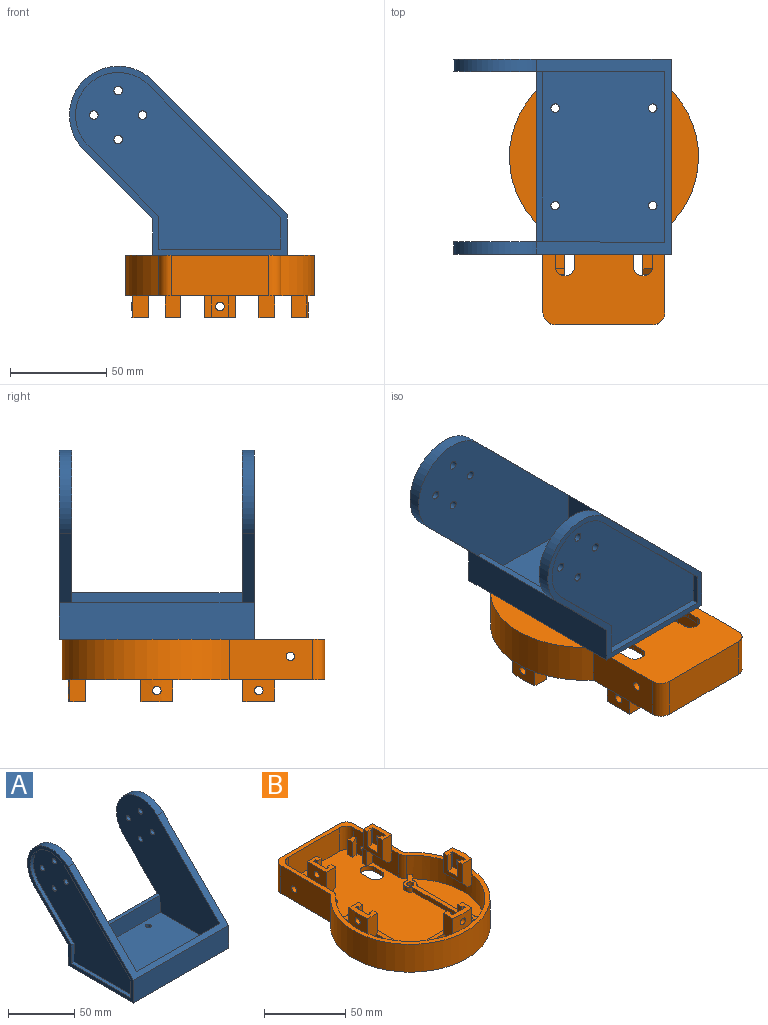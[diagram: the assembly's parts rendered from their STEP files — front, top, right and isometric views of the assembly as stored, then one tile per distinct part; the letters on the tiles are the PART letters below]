
ASSEMBLY  parts=2 mates=1
PART A: 42 faces, bbox 101.5x113.3x98.4 mm
  f0: plane 106.95x92.08mm, normal (-1,0,0), area 5115.5mm2, adj f15,f16,f17,f18,f35,f36,f37,f38
  f1: plane 101.47x69.94mm, normal (0,-0.71,0.71), area 1654.8mm2, adj f6,f9,f12,f13,f23,f24,f34,f41
  f2: plane 36.01x36.01mm, normal (0,0.71,-0.71), area 323.4mm2, adj f6,f9,f27,f34
  f3: cylinder r=2.22mm len=4.45mm, axis (-1,0,0), area 44.3mm2, adj f8,f9
  f4: cylinder r=2.22mm len=4.45mm, axis (-1,0,0), area 44.3mm2, adj f8,f9
  f5: cylinder r=2.22mm len=4.45mm, axis (-1,0,0), area 44.3mm2, adj f8,f9
  f6: cylinder r=25.4mm len=43.36mm, axis (-1,0,0), area 506.7mm2, adj f1,f2,f9,f34
  f7: cylinder r=2.22mm len=4.45mm, axis (-1,0,0), area 44.3mm2, adj f8,f9
  f8: plane 106.95x92.08mm, normal (1,0,0), area 5115.5mm2, adj f3,f4,f5,f7,f28,f29,f30,f31
  f9: plane 110.13x95.25mm, normal (-1,0,0), area 5823.7mm2, adj f1,f2,f3,f4,f5,f6,f7,f10
  f10: plane 88.77x63.5mm, normal (0,0,1), area 5575mm2, adj f9,f12,f19,f20,f21,f22,f23,f25
  f11: plane 101.47x69.85mm, normal (0,0,-1), area 7025.8mm2, adj f19,f20,f21,f22,f24,f27,f34,f41
  f12: plane 110.13x95.25mm, normal (1,0,0), area 5823.7mm2, adj f1,f10,f13,f14,f15,f16,f17,f18
  f13: cylinder r=25.4mm len=43.36mm, axis (-1,0,0), area 506.7mm2, adj f1,f12,f14,f41
  f14: plane 36.01x36.01mm, normal (0,0.71,-0.71), area 323.4mm2, adj f12,f13,f27,f41
  f15: cylinder r=2.22mm len=4.45mm, axis (-1,0,0), area 44.3mm2, adj f0,f12
  f16: cylinder r=2.22mm len=4.45mm, axis (-1,0,0), area 44.3mm2, adj f0,f12
  f17: cylinder r=2.22mm len=4.45mm, axis (-1,0,0), area 44.3mm2, adj f0,f12
  f18: cylinder r=2.22mm len=4.45mm, axis (-1,0,0), area 44.3mm2, adj f0,f12
  f19: cylinder r=2.22mm len=4.45mm, axis (0,0,1), area 44.3mm2, adj f10,f11
  f20: cylinder r=2.22mm len=4.45mm, axis (0,0,1), area 44.3mm2, adj f10,f11
  f21: cylinder r=2.22mm len=4.45mm, axis (0,0,1), area 44.3mm2, adj f10,f11
  f22: cylinder r=2.22mm len=4.45mm, axis (0,0,1), area 44.3mm2, adj f10,f11
  f23: plane 88.77x21.04mm, normal (0,1,0), area 1868mm2, adj f1,f9,f10,f12
  f24: plane 101.47x21.04mm, normal (0,-1,0), area 2135.2mm2, adj f1,f11,f34,f41
  f25: plane 88.77x15.88mm, normal (0,-1,0), area 1409.3mm2, adj f9,f10,f12,f26
  f26: plane 88.77x3.18mm, normal (0,0,1), area 281.9mm2, adj f9,f12,f25,f27
  f27: plane 101.47x19.05mm, normal (0,1,0), area 1933.1mm2, adj f2,f11,f14,f26,f34,f41
  f28: plane 36.94x36.94mm, normal (0,-0.71,0.71), area 165.9mm2, adj f8,f29,f33,f34
  f29: plane 17.19x3.18mm, normal (0,-1,0), area 54.6mm2, adj f8,f28,f30,f34
  f30: plane 63.5x3.18mm, normal (0,0,1), area 201.6mm2, adj f8,f29,f31,f34
  f31: plane 16.55x3.18mm, normal (0,1,0), area 52.6mm2, adj f8,f30,f32,f34
  f32: plane 69.01x69.01mm, normal (0,0.71,-0.71), area 309.9mm2, adj f8,f31,f33,f34
  f33: cylinder r=22.23mm len=37.94mm, axis (-1,0,0), area 221.7mm2, adj f8,f28,f32,f34
  f34: plane 113.3x98.43mm, normal (1,0,0), area 1042.2mm2, adj f1,f2,f6,f11,f24,f27,f28,f29
  f35: plane 17.19x3.18mm, normal (0,-1,0), area 54.6mm2, adj f0,f36,f40,f41
  f36: plane 36.94x36.94mm, normal (0,-0.71,0.71), area 165.9mm2, adj f0,f35,f37,f41
  f37: cylinder r=22.23mm len=37.94mm, axis (1,0,0), area 221.7mm2, adj f0,f36,f38,f41
  f38: plane 69.01x69.01mm, normal (0,0.71,-0.71), area 309.9mm2, adj f0,f37,f39,f41
  f39: plane 16.55x3.18mm, normal (0,1,0), area 52.6mm2, adj f0,f38,f40,f41
  f40: plane 63.5x3.18mm, normal (0,0,1), area 201.6mm2, adj f0,f35,f39,f41
  f41: plane 113.3x98.43mm, normal (-1,0,0), area 1042.2mm2, adj f1,f11,f13,f14,f24,f27,f35,f36
PART B: 190 faces, bbox 98.4x136.6x32.4 mm
  f0: plane 11.43x5.08mm, normal (0,0,1), area 49.7mm2, adj f7,f176,f178,f179,f180,f181,f182,f183
  f1: plane 136.59x98.43mm, normal (0,0,1), area 1242.6mm2, adj f11,f13,f15,f19,f20,f21,f25,f28
  f2: plane 11.43x5.08mm, normal (0,0,1), area 49.7mm2, adj f97,f167,f169,f170,f171,f172,f173,f174
  f3: plane 11.43x5.08mm, normal (0,0,1), area 49.7mm2, adj f9,f158,f160,f161,f162,f163,f164,f165
  f4: plane 11.43x5.08mm, normal (0,0,1), area 49.7mm2, adj f107,f149,f151,f152,f153,f154,f155,f156
  f5: plane 11.43x5.08mm, normal (0,0,1), area 49.7mm2, adj f10,f140,f142,f143,f144,f145,f146,f147
  f6: plane 3.18x3.18mm, normal (0,0,-1), area 10.1mm2, adj f11,f99,f128,f138
  f7: plane 16.51x14.61mm, normal (-1,0,0), area 139.5mm2, adj f0,f99,f100,f129,f138,f139,f176,f178
  f8: plane 3.18x3.18mm, normal (0,0,-1), area 10.1mm2, adj f13,f77,f125,f137
  f9: plane 16.51x14.61mm, normal (-1,0,0), area 139.5mm2, adj f3,f109,f110,f118,f130,f131,f158,f160
  f10: plane 16.51x14.61mm, normal (1,0,0), area 139.5mm2, adj f5,f102,f103,f113,f134,f135,f140,f142
  f11: plane 22.29x17.78mm, normal (-1,0,0), area 311.7mm2, adj f1,f6,f12,f14,f34,f99,f101,f127
  f12: plane 11.43x5.08mm, normal (0,-1,0), area 50.2mm2, adj f11,f14,f85,f101,f139
  f13: plane 22.29x17.78mm, normal (1,0,0), area 311.7mm2, adj f1,f8,f14,f33,f77,f96,f98,f124
  f14: plane 108.01x62.82mm, normal (0,0,1), area 5270.4mm2, adj f11,f12,f13,f15,f28,f29,f30,f31
  f15: plane 17.78x16.51mm, normal (-1,0,0), area 220mm2, adj f1,f14,f31,f82,f86,f87,f92,f94
  f16: plane 136.59x98.43mm, normal (0,0,-1), area 9894.2mm2, adj f19,f20,f21,f22,f23,f24,f25,f26
  f17: plane 62.82x19.05mm, normal (0,0,1), area 892.1mm2, adj f28,f37,f38,f39,f40,f41
  f18: plane 62.82x19.05mm, normal (0,0,1), area 892.1mm2, adj f28,f42,f43,f44,f45,f46
  f19: plane 43.43x20.96mm, normal (-1,0,0), area 894.5mm2, adj f1,f16,f20,f36,f93
  f20: cylinder r=49.21mm len=98.43mm, axis (0,0,-1), area 5033.2mm2, adj f1,f16,f19,f21
  f21: plane 43.43x20.96mm, normal (1,0,0), area 894.5mm2, adj f1,f16,f20,f35,f94
  f22: cylinder r=2.22mm len=6.35mm, axis (0,0,-1), area 88.7mm2, adj f16,f61
  f23: cylinder r=2.22mm len=6.35mm, axis (0,0,-1), area 88.7mm2, adj f16,f61
  f24: cylinder r=2.22mm len=6.35mm, axis (0,0,-1), area 88.7mm2, adj f16,f61
  f25: plane 50.8x20.96mm, normal (0,1,0), area 1064.5mm2, adj f1,f16,f35,f36
  f26: cylinder r=2.22mm len=6.35mm, axis (0,0,-1), area 88.7mm2, adj f16,f61
  f27: plane 62.82x19.05mm, normal (0,0,1), area 892.1mm2, adj f28,f56,f57,f58,f59,f60
  f28: cylinder r=46.04mm len=92.08mm, axis (0,0,-1), area 3497mm2, adj f1,f14,f17,f18,f27,f33,f34,f37
  f29: plane 17.78x16.51mm, normal (1,0,0), area 220mm2, adj f1,f14,f32,f71,f75,f76,f81,f93
  f30: plane 44.45x17.78mm, normal (0,-1,0), area 790.3mm2, adj f1,f14,f31,f32
  f31: cylinder r=6.35mm len=17.78mm, axis (0,0,1), area 177.3mm2, adj f1,f14,f15,f30,f88
  f32: cylinder r=6.35mm len=17.78mm, axis (0,0,-1), area 177.3mm2, adj f1,f14,f29,f30,f70
  f33: cylinder r=6.35mm len=17.78mm, axis (0,0,-1), area 95mm2, adj f1,f13,f14,f28
  f34: cylinder r=6.35mm len=17.78mm, axis (0,0,-1), area 95mm2, adj f1,f11,f14,f28
  f35: cylinder r=6.35mm len=20.96mm, axis (0,0,1), area 209mm2, adj f1,f16,f21,f25
  f36: cylinder r=6.35mm len=20.96mm, axis (0,0,-1), area 209mm2, adj f1,f16,f19,f25
  f37: plane 4.44x4.44mm, normal (0.71,-0.71,0), area 19.9mm2, adj f17,f28,f38,f61
  f38: cylinder r=4.13mm len=5.38mm, axis (0,0,-1), area 20.5mm2, adj f17,f37,f39,f61
  f39: plane 43.18x3.18mm, normal (0,-1,0), area 137.1mm2, adj f17,f38,f40,f61
  f40: cylinder r=4.13mm len=5.38mm, axis (0,0,-1), area 20.5mm2, adj f17,f39,f41,f61
  f41: plane 4.44x4.44mm, normal (-0.71,-0.71,0), area 19.9mm2, adj f17,f28,f40,f61
  f42: plane 4.44x4.44mm, normal (0.71,0.71,0), area 19.9mm2, adj f18,f28,f43,f61
  f43: cylinder r=4.13mm len=5.38mm, axis (0,0,-1), area 20.5mm2, adj f18,f42,f44,f61
  f44: plane 43.18x3.18mm, normal (1,0,0), area 137.1mm2, adj f18,f43,f45,f61
  f45: cylinder r=4.13mm len=5.38mm, axis (0,0,-1), area 20.5mm2, adj f18,f44,f46,f61
  f46: plane 4.44x4.44mm, normal (0.71,-0.71,0), area 19.9mm2, adj f18,f28,f45,f61
  f47: plane 4.44x4.44mm, normal (-0.71,0.71,0), area 19.9mm2, adj f14,f28,f48,f61
  f48: cylinder r=4.13mm len=7.94mm, axis (0,0,-1), area 41.1mm2, adj f14,f47,f49,f61
  f49: plane 43.18x3.18mm, normal (-1,0,0), area 137.1mm2, adj f14,f48,f50,f61
  f50: cylinder r=4.13mm len=3.18mm, axis (0,0,-1), area 10.2mm2, adj f14,f49,f51,f61
  f51: plane 43.18x3.18mm, normal (0,1,0), area 137.1mm2, adj f14,f50,f52,f61
  f52: cylinder r=4.13mm len=3.18mm, axis (0,0,-1), area 10.2mm2, adj f14,f51,f53,f61
  f53: plane 43.18x3.18mm, normal (1,0,0), area 137.1mm2, adj f14,f52,f54,f61
  f54: cylinder r=4.13mm len=7.94mm, axis (0,0,-1), area 41.1mm2, adj f14,f53,f55,f61
  f55: plane 4.44x4.44mm, normal (0.71,0.71,0), area 19.9mm2, adj f14,f28,f54,f61
  f56: plane 4.44x4.44mm, normal (-0.71,-0.71,0), area 19.9mm2, adj f27,f28,f57,f61
  f57: cylinder r=4.13mm len=5.38mm, axis (0,0,-1), area 20.5mm2, adj f27,f56,f58,f61
  f58: plane 43.18x3.18mm, normal (-1,0,0), area 137.1mm2, adj f27,f57,f59,f61
  f59: cylinder r=4.13mm len=5.38mm, axis (0,0,-1), area 20.5mm2, adj f27,f58,f60,f61
  f60: plane 4.44x4.44mm, normal (-0.71,0.71,0), area 19.9mm2, adj f27,f28,f59,f61
  f61: plane 67.31x67.31mm, normal (0,0,1), area 636.5mm2, adj f22,f23,f24,f26,f28,f37,f38,f39
  f62: plane 6.35x3.18mm, normal (1,0,0), area 20.2mm2, adj f14,f16,f66,f67
  f63: plane 6.35x3.18mm, normal (-1,0,0), area 20.2mm2, adj f14,f16,f66,f67
  f64: plane 6.35x3.18mm, normal (1,0,0), area 20.2mm2, adj f14,f16,f68,f69
  f65: plane 6.35x3.18mm, normal (-1,0,0), area 20.2mm2, adj f14,f16,f68,f69
  f66: cylinder r=5.08mm len=10.16mm, axis (0,0,-1), area 50.7mm2, adj f14,f16,f62,f63
  f67: cylinder r=5.08mm len=10.16mm, axis (0,0,1), area 50.7mm2, adj f14,f16,f62,f63
  f68: cylinder r=5.08mm len=10.16mm, axis (0,0,1), area 50.7mm2, adj f14,f16,f64,f65
  f69: cylinder r=5.08mm len=10.16mm, axis (0,0,-1), area 50.7mm2, adj f14,f16,f64,f65
  f70: plane 11.43x5.08mm, normal (0,1,0), area 58.1mm2, adj f14,f32,f74,f75
  f71: plane 11.43x1.78mm, normal (0,-1,0), area 20.3mm2, adj f14,f29,f72,f75
  f72: plane 11.43x1.27mm, normal (-1,0,0), area 14.5mm2, adj f14,f71,f73,f75
  f73: plane 11.43x3.3mm, normal (0,-1,0), area 37.7mm2, adj f14,f72,f74,f75
  f74: plane 11.43x3.81mm, normal (1,0,0), area 43.5mm2, adj f14,f70,f73,f75
  f75: plane 5.08x3.81mm, normal (0,0,1), area 17.1mm2, adj f29,f70,f71,f72,f73,f74
  f76: plane 11.43x1.78mm, normal (0,1,0), area 20.3mm2, adj f14,f29,f80,f81
  f77: plane 11.43x5.08mm, normal (0,-1,0), area 50.2mm2, adj f8,f13,f14,f78,f137
  f78: plane 11.43x3.81mm, normal (1,0,0), area 43.5mm2, adj f14,f77,f79,f81
  f79: plane 11.43x3.3mm, normal (0,1,0), area 37.7mm2, adj f14,f78,f80,f81
  f80: plane 11.43x1.27mm, normal (-1,0,0), area 14.5mm2, adj f14,f76,f79,f81
  f81: plane 5.08x3.81mm, normal (0,0,1), area 17.1mm2, adj f29,f76,f78,f79,f80,f95
  f82: plane 11.43x1.78mm, normal (0,1,0), area 20.3mm2, adj f14,f15,f83,f86
  f83: plane 11.43x1.27mm, normal (1,0,0), area 14.5mm2, adj f14,f82,f84,f86
  f84: plane 11.43x3.3mm, normal (0,1,0), area 37.7mm2, adj f14,f83,f85,f86
  f85: plane 11.43x3.81mm, normal (-1,0,0), area 43.5mm2, adj f12,f14,f84,f86
  f86: plane 5.08x3.81mm, normal (0,0,1), area 17.1mm2, adj f15,f82,f83,f84,f85,f100
  f87: plane 11.43x1.78mm, normal (0,-1,0), area 20.3mm2, adj f14,f15,f91,f92
  f88: plane 11.43x5.08mm, normal (0,1,0), area 58.1mm2, adj f14,f31,f89,f92
  f89: plane 11.43x3.81mm, normal (-1,0,0), area 43.5mm2, adj f14,f88,f90,f92
  f90: plane 11.43x3.3mm, normal (0,-1,0), area 37.7mm2, adj f14,f89,f91,f92
  f91: plane 11.43x1.27mm, normal (1,0,0), area 14.5mm2, adj f14,f87,f90,f92
  f92: plane 5.08x3.81mm, normal (0,0,1), area 17.1mm2, adj f15,f87,f88,f89,f90,f91
  f93: cylinder r=2.22mm len=4.45mm, axis (-1,0,0), area 44.3mm2, adj f19,f29
  f94: cylinder r=2.22mm len=4.45mm, axis (-1,0,0), area 44.3mm2, adj f15,f21
  f95: plane 17.78x8.26mm, normal (0,1,0), area 141.7mm2, adj f29,f81,f97,f137,f168,f175
  f96: plane 19.69x8.26mm, normal (0,-1,0), area 149.6mm2, adj f13,f97,f98,f136,f168,f175
  f97: plane 16.51x14.61mm, normal (1,0,0), area 139.5mm2, adj f2,f95,f96,f126,f136,f137,f167,f169
  f98: plane 3.18x3.18mm, normal (0,0,-1), area 10.1mm2, adj f13,f96,f124,f136
  f99: plane 19.69x8.26mm, normal (0,-1,0), area 149.6mm2, adj f6,f7,f11,f138,f177,f184
  f100: plane 17.78x8.26mm, normal (0,1,0), area 141.7mm2, adj f7,f15,f86,f139,f177,f184
  f101: plane 3.18x3.18mm, normal (0,0,-1), area 10.1mm2, adj f11,f12,f127,f139
  f102: plane 19.69x8.26mm, normal (0,-1,0), area 149.6mm2, adj f10,f28,f104,f134,f141,f148
  f103: plane 19.69x8.26mm, normal (0,1,0), area 149.6mm2, adj f10,f28,f104,f135,f141,f148
  f104: plane 16.51x3.92mm, normal (0,0,-1), area 28.4mm2, adj f28,f102,f103,f112,f114,f115,f134,f135
  f105: plane 19.69x8.26mm, normal (-1,0,0), area 149.6mm2, adj f28,f107,f108,f133,f150,f157
  f106: plane 19.69x8.26mm, normal (1,0,0), area 149.6mm2, adj f28,f107,f108,f132,f150,f157
  f107: plane 16.51x14.61mm, normal (0,1,0), area 139.5mm2, adj f4,f105,f106,f122,f132,f133,f149,f151
  f108: plane 16.51x3.92mm, normal (0,0,-1), area 28.4mm2, adj f28,f105,f106,f120,f121,f123,f132,f133
  f109: plane 19.69x8.26mm, normal (0,1,0), area 149.6mm2, adj f9,f28,f111,f131,f159,f166
  f110: plane 19.69x8.26mm, normal (0,-1,0), area 149.6mm2, adj f9,f28,f111,f130,f159,f166
  f111: plane 16.51x3.92mm, normal (0,0,-1), area 28.4mm2, adj f28,f109,f110,f116,f117,f119,f130,f131
  f112: plane 8.26x5.08mm, normal (0,-1,0), area 29mm2, adj f104,f113,f115,f135
  f113: plane 10.16x8.26mm, normal (0,0,-1), area 83.9mm2, adj f10,f112,f114,f115
  f114: plane 8.26x5.08mm, normal (0,1,0), area 29mm2, adj f104,f113,f115,f134
  f115: plane 10.16x5.08mm, normal (1,0,0), area 51.6mm2, adj f104,f112,f113,f114
  f116: plane 8.26x5.08mm, normal (0,-1,0), area 29mm2, adj f111,f118,f119,f131
  f117: plane 8.26x5.08mm, normal (0,1,0), area 29mm2, adj f111,f118,f119,f130
  f118: plane 10.16x8.26mm, normal (0,0,-1), area 83.9mm2, adj f9,f116,f117,f119
  f119: plane 10.16x5.08mm, normal (-1,0,0), area 51.6mm2, adj f111,f116,f117,f118
  f120: plane 8.26x5.08mm, normal (-1,0,0), area 29mm2, adj f108,f122,f123,f132
  f121: plane 8.26x5.08mm, normal (1,0,0), area 29mm2, adj f108,f122,f123,f133
  f122: plane 10.16x8.26mm, normal (0,0,-1), area 83.9mm2, adj f107,f120,f121,f123
  f123: plane 10.16x5.08mm, normal (0,1,0), area 51.6mm2, adj f108,f120,f121,f122
  f124: plane 8.26x5.08mm, normal (0,1,0), area 29mm2, adj f13,f98,f126,f136
  f125: plane 8.26x5.08mm, normal (0,-1,0), area 29mm2, adj f8,f13,f126,f137
  f126: plane 10.16x8.26mm, normal (0,0,-1), area 83.9mm2, adj f13,f97,f124,f125
  f127: plane 8.26x5.08mm, normal (0,-1,0), area 29mm2, adj f11,f101,f129,f139
  f128: plane 8.26x5.08mm, normal (0,1,0), area 29mm2, adj f6,f11,f129,f138
  f129: plane 10.16x8.26mm, normal (0,0,-1), area 83.9mm2, adj f7,f11,f127,f128
  f130: plane 5.08x5.08mm, normal (-0.71,0,-0.71), area 22.8mm2, adj f9,f110,f111,f117
  f131: plane 5.08x5.08mm, normal (-0.71,0,-0.71), area 22.8mm2, adj f9,f109,f111,f116
  f132: plane 5.08x5.08mm, normal (0,0.71,-0.71), area 22.8mm2, adj f106,f107,f108,f120
  f133: plane 5.08x5.08mm, normal (0,0.71,-0.71), area 22.8mm2, adj f105,f107,f108,f121
  f134: plane 5.08x5.08mm, normal (0.71,0,-0.71), area 22.8mm2, adj f10,f102,f104,f114
  f135: plane 5.08x5.08mm, normal (0.71,0,-0.71), area 22.8mm2, adj f10,f103,f104,f112
  f136: plane 5.08x5.08mm, normal (0.71,0,-0.71), area 22.8mm2, adj f96,f97,f98,f124
  f137: plane 5.08x5.08mm, normal (0.71,0,-0.71), area 22.8mm2, adj f8,f77,f95,f97,f125
  f138: plane 5.08x5.08mm, normal (-0.71,0,-0.71), area 22.8mm2, adj f6,f7,f99,f128
  f139: plane 5.08x5.08mm, normal (-0.71,0,-0.71), area 22.8mm2, adj f7,f12,f100,f101,f127
  f140: plane 11.43x3.3mm, normal (0,-1,0), area 37.7mm2, adj f5,f10,f147,f148
  f141: cylinder r=46.04mm len=16.51mm, axis (0,0,-1), area 174.2mm2, adj f1,f102,f103,f148,f188
  f142: plane 11.43x3.3mm, normal (0,1,0), area 37.7mm2, adj f5,f10,f143,f148
  f143: plane 11.43x1.27mm, normal (-1,0,0), area 14.5mm2, adj f5,f142,f144,f148
  f144: plane 11.43x1.78mm, normal (0,1,0), area 20.3mm2, adj f5,f143,f145,f148
  f145: plane 11.43x11.43mm, normal (1,0,0), area 115.1mm2, adj f5,f144,f146,f148,f188
  f146: plane 11.43x1.78mm, normal (0,-1,0), area 20.3mm2, adj f5,f145,f147,f148
  f147: plane 11.43x1.27mm, normal (-1,0,0), area 14.5mm2, adj f5,f140,f146,f148
  f148: plane 16.51x9mm, normal (0,0,1), area 94.8mm2, adj f10,f102,f103,f140,f141,f142,f143,f144
  f149: plane 11.43x3.3mm, normal (1,0,0), area 37.7mm2, adj f4,f107,f156,f157
  f150: cylinder r=46.04mm len=16.51mm, axis (0,0,-1), area 174.2mm2, adj f1,f105,f106,f157,f189
  f151: plane 11.43x3.3mm, normal (-1,0,0), area 37.7mm2, adj f4,f107,f152,f157
  f152: plane 11.43x1.27mm, normal (0,-1,0), area 14.5mm2, adj f4,f151,f153,f157
  f153: plane 11.43x1.78mm, normal (-1,0,0), area 20.3mm2, adj f4,f152,f154,f157
  f154: plane 11.43x11.43mm, normal (0,1,0), area 115.1mm2, adj f4,f153,f155,f157,f189
  f155: plane 11.43x1.78mm, normal (1,0,0), area 20.3mm2, adj f4,f154,f156,f157
  f156: plane 11.43x1.27mm, normal (0,-1,0), area 14.5mm2, adj f4,f149,f155,f157
  f157: plane 16.51x9mm, normal (0,0,1), area 94.8mm2, adj f105,f106,f107,f149,f150,f151,f152,f153
  f158: plane 11.43x3.3mm, normal (0,1,0), area 37.7mm2, adj f3,f9,f165,f166
  f159: cylinder r=46.04mm len=16.51mm, axis (0,0,-1), area 174.2mm2, adj f1,f109,f110,f166,f187
  f160: plane 11.43x3.3mm, normal (0,-1,0), area 37.7mm2, adj f3,f9,f161,f166
  f161: plane 11.43x1.27mm, normal (1,0,0), area 14.5mm2, adj f3,f160,f162,f166
  f162: plane 11.43x1.78mm, normal (0,-1,0), area 20.3mm2, adj f3,f161,f163,f166
  f163: plane 11.43x11.43mm, normal (-1,0,0), area 115.1mm2, adj f3,f162,f164,f166,f187
  f164: plane 11.43x1.78mm, normal (0,1,0), area 20.3mm2, adj f3,f163,f165,f166
  f165: plane 11.43x1.27mm, normal (1,0,0), area 14.5mm2, adj f3,f158,f164,f166
  f166: plane 16.51x9mm, normal (0,0,1), area 94.8mm2, adj f9,f109,f110,f158,f159,f160,f161,f162
  f167: plane 11.43x3.3mm, normal (0,-1,0), area 37.7mm2, adj f2,f97,f174,f175
  f168: plane 16.51x11.43mm, normal (-1,0,0), area 173.2mm2, adj f1,f95,f96,f175,f186
  f169: plane 11.43x3.3mm, normal (0,1,0), area 37.7mm2, adj f2,f97,f170,f175
  f170: plane 11.43x1.27mm, normal (-1,0,0), area 14.5mm2, adj f2,f169,f171,f175
  f171: plane 11.43x1.78mm, normal (0,1,0), area 20.3mm2, adj f2,f170,f172,f175
  f172: plane 11.43x11.43mm, normal (1,0,0), area 115.1mm2, adj f2,f171,f173,f175,f186
  f173: plane 11.43x1.78mm, normal (0,-1,0), area 20.3mm2, adj f2,f172,f174,f175
  f174: plane 11.43x1.27mm, normal (-1,0,0), area 14.5mm2, adj f2,f167,f173,f175
  f175: plane 16.51x8.26mm, normal (0,0,1), area 86.6mm2, adj f95,f96,f97,f167,f168,f169,f170,f171
  f176: plane 11.43x3.3mm, normal (0,1,0), area 37.7mm2, adj f0,f7,f183,f184
  f177: plane 16.51x11.43mm, normal (1,0,0), area 173.2mm2, adj f1,f99,f100,f184,f185
  f178: plane 11.43x3.3mm, normal (0,-1,0), area 37.7mm2, adj f0,f7,f179,f184
  f179: plane 11.43x1.27mm, normal (1,0,0), area 14.5mm2, adj f0,f178,f180,f184
  f180: plane 11.43x1.78mm, normal (0,-1,0), area 20.3mm2, adj f0,f179,f181,f184
  f181: plane 11.43x11.43mm, normal (-1,0,0), area 115.1mm2, adj f0,f180,f182,f184,f185
  f182: plane 11.43x1.78mm, normal (0,1,0), area 20.3mm2, adj f0,f181,f183,f184
  f183: plane 11.43x1.27mm, normal (1,0,0), area 14.5mm2, adj f0,f176,f182,f184
  f184: plane 16.51x8.26mm, normal (0,0,1), area 86.6mm2, adj f7,f99,f100,f176,f177,f178,f179,f180
  f185: cylinder r=2.22mm len=4.45mm, axis (1,0,0), area 44.3mm2, adj f177,f181
  f186: cylinder r=2.22mm len=4.45mm, axis (1,0,0), area 44.3mm2, adj f168,f172
  f187: cylinder r=2.22mm len=4.45mm, axis (1,0,0), area 54.4mm2, adj f159,f163
  f188: cylinder r=2.22mm len=4.45mm, axis (1,0,0), area 54.4mm2, adj f141,f145
  f189: cylinder r=2.22mm len=4.45mm, axis (0,1,0), area 54.4mm2, adj f150,f154
PLACE A rot(axis=(0,0,1),90deg) t=(0,44.96,0)mm
PLACE B rot(axis=(1,0,0),180deg) t=(52.98,0.57,-73.03)mm
MATE fastened B.f23 <-> A.f22  axis (0,0,1) through (78.38,-24.83,-73.03)mm
